# Revit family: DSI-FW119_Smoke-and-Fire-Curtain_Over-Under-Headbox_Door-Systems
name_source: partatom
category: Doors
units: mm (PartAtom-declared; Revit-internal decimal feet)

## family parameters
Always vertical = Yes
Cut with Voids When Loaded = No
Host = Wall
OmniClass Number = 23.30.60.17
OmniClass Title = Fire and Smoke Shutters and Curtains
Room Calculation Point = No
Shared = No

## types (1)
- Default
    CAD Details = https://www.arcat.com
    Curtain Finish = HS690-SS FABRIC- FW119
    CurtainDrop_Viz = Yes
    Frame Finish = Metal - Steel - Primed
    Frame Projection Ext. = 0' - 1"
    Frame Projection Int. = 0' - 1"
    Frame Width = 0' - 3"
    Height = 9' - 0"
    Jamb Depth = 0' - 3"
    Jamb Lenght = 0' - 4"
    Keynote = 08 33 44
    Manufacturer = Door Systems
    Model = DSI-FW119
    Product Page URL = https://www.arcat.com
    Specification = https://www.arcat.com
    URL = https://www.doorsysinc.com
    Wall Closure = By host
    Width = 9' - 0"

## geometry (parser evidence)
native form markers: Sweep x7
no freeform markers — native parametric forms only
